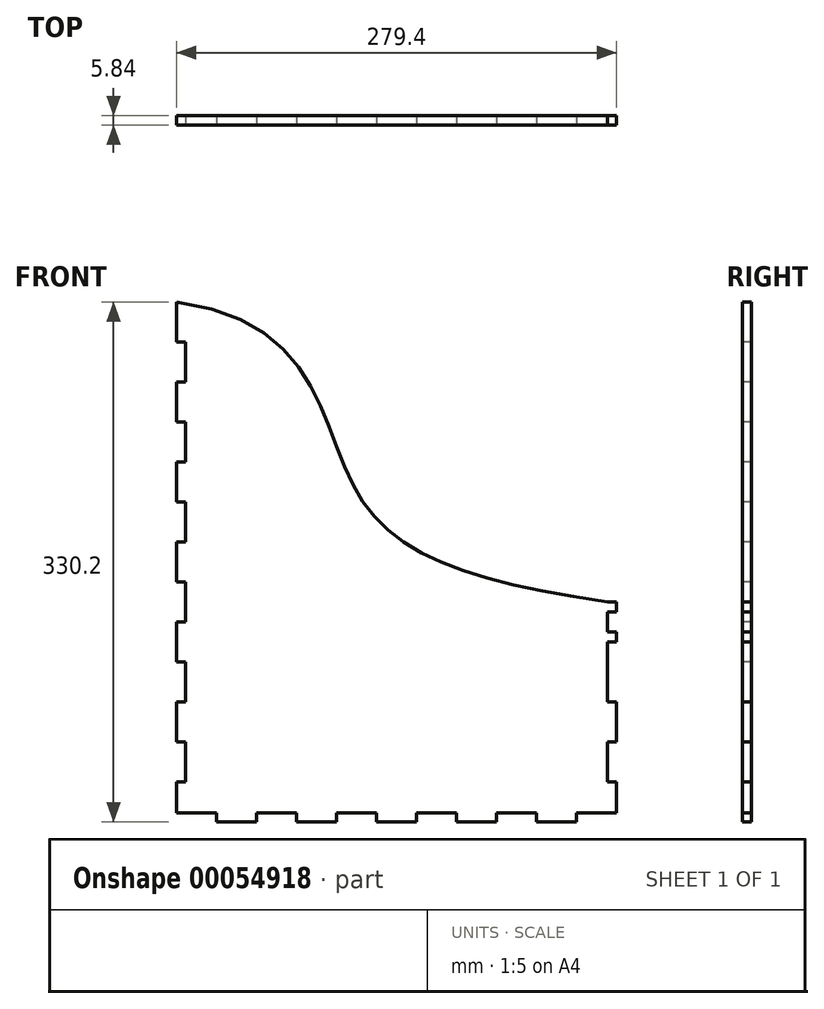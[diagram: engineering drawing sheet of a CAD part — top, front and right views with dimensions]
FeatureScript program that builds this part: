
annotation { "Feature Type Name" : "Feature", "Feature Type Description" : "" }
export const myFeature = defineFeature(function(context is Context, id is Id, definition is map)
    precondition{}
    {
        {
            var Q0;
            Q0=qCreatedBy(makeId("Front.planeOp"),FACE);
            var sketch = newSketch(context, id + "F0", { "sketchPlane" : qUnion([Q0])});
            skLineSegment(sketch, "E0.bottom", {"start": v(-113.95, 205.98) * mm, "end": v(165.45, 205.98) * mm});
            skLineSegment(sketch, "E0.top", {"start": v(-113.95, -124.22) * mm, "end": v(165.45, -124.22) * mm});
            skLineSegment(sketch, "E0.left", {"start": v(-113.95, 205.98) * mm, "end": v(-113.95, -124.22) * mm});
            skLineSegment(sketch, "E0.right", {"start": v(165.45, 205.98) * mm, "end": v(165.45, -124.22) * mm});
            skSolve(sketch);
        }
        {
            var Q0;
            Q0=makeQuery(id+"F0.imprint","IMPRINT",FACE,{"disambiguationData":[TD([[makeQuery(id+"F0.imprint","IMPRINT",EDGE,{"derivedFrom":sQuery(id+"F0.wireOp",EDGE,"E0.bottom")}),-1.0]])]});
            extrude(context, id + "F1", {"entities" : qUnion([Q0]), "depth" : 5.84 * mm});
        }
        {
            var Q0;
            Q0=makeQuery(id+"F1.opExtrude","CAP_FACE",FACE,{"disambiguationData":[OSD([sQuery(id+"F0.wireOp",EDGE,"E0.bottom"),sQuery(id+"F0.wireOp",EDGE,"E0.top"),sQuery(id+"F0.wireOp",EDGE,"E0.left"),sQuery(id+"F0.wireOp",EDGE,"E0.right")])],"isStart":false});
            var sketch = newSketch(context, id + "F2", { "sketchPlane" : qUnion([Q0])});
            skLineSegment(sketch, "E1", {"start": v(165.45, -118.38) * mm, "end": v(140.05, -118.38) * mm});
            skLineSegment(sketch, "E2", {"start": v(140.05, -118.38) * mm, "end": v(140.05, -124.22) * mm});
            skLineSegment(sketch, "E3", {"start": v(140.05, -124.22) * mm, "end": v(114.65, -124.22) * mm});
            skLineSegment(sketch, "E4", {"start": v(114.65, -124.22) * mm, "end": v(114.65, -118.38) * mm});
            skLineSegment(sketch, "E5", {"start": v(114.65, -118.38) * mm, "end": v(89.25, -118.38) * mm});
            skLineSegment(sketch, "E6", {"start": v(89.25, -118.38) * mm, "end": v(89.25, -124.22) * mm});
            skLineSegment(sketch, "E7", {"start": v(89.25, -124.22) * mm, "end": v(63.85, -124.22) * mm});
            skLineSegment(sketch, "E8", {"start": v(63.85, -124.22) * mm, "end": v(63.85, -118.38) * mm});
            skLineSegment(sketch, "E9", {"start": v(63.85, -118.38) * mm, "end": v(38.45, -118.38) * mm});
            skLineSegment(sketch, "E10", {"start": v(38.45, -118.38) * mm, "end": v(38.45, -124.22) * mm});
            skLineSegment(sketch, "E11", {"start": v(38.45, -124.22) * mm, "end": v(13.05, -124.22) * mm});
            skLineSegment(sketch, "E12", {"start": v(13.05, -124.22) * mm, "end": v(13.05, -118.38) * mm});
            skLineSegment(sketch, "E13", {"start": v(13.05, -118.38) * mm, "end": v(-12.35, -118.38) * mm});
            skLineSegment(sketch, "E14", {"start": v(-12.35, -118.38) * mm, "end": v(-12.35, -124.22) * mm});
            skLineSegment(sketch, "E15", {"start": v(-12.35, -124.22) * mm, "end": v(-37.75, -124.22) * mm});
            skLineSegment(sketch, "E16", {"start": v(-37.75, -124.22) * mm, "end": v(-37.75, -118.38) * mm});
            skLineSegment(sketch, "E17", {"start": v(-37.75, -118.38) * mm, "end": v(-113.95, -118.38) * mm});
            skLineSegment(sketch, "E18", {"start": v(-113.95, -118.38) * mm, "end": v(-113.95, -124.22) * mm});
            skLineSegment(sketch, "E19", {"start": v(-113.95, -124.22) * mm, "end": v(-37.75, -124.22) * mm});
            skLineSegment(sketch, "E20.bottom", {"start": v(165.45, -98.82) * mm, "end": v(159.6, -98.82) * mm});
            skLineSegment(sketch, "E20.top", {"start": v(165.45, -73.42) * mm, "end": v(159.6, -73.42) * mm});
            skLineSegment(sketch, "E20.left", {"start": v(165.45, -98.82) * mm, "end": v(165.45, -73.42) * mm});
            skLineSegment(sketch, "E20.right", {"start": v(159.6, -98.82) * mm, "end": v(159.6, -73.42) * mm});
            skLineSegment(sketch, "E21.bottom", {"start": v(165.45, -48.02) * mm, "end": v(159.6, -48.02) * mm});
            skLineSegment(sketch, "E21.top", {"start": v(165.45, -9.92) * mm, "end": v(159.6, -9.92) * mm});
            skLineSegment(sketch, "E21.left", {"start": v(165.45, -48.02) * mm, "end": v(165.45, -9.92) * mm});
            skLineSegment(sketch, "E21.right", {"start": v(159.6, -48.02) * mm, "end": v(159.6, -9.92) * mm});
            skLineSegment(sketch, "E22.bottom", {"start": v(-113.95, -98.82) * mm, "end": v(-108.1, -98.82) * mm});
            skLineSegment(sketch, "E22.top", {"start": v(-113.95, -73.42) * mm, "end": v(-108.1, -73.42) * mm});
            skLineSegment(sketch, "E22.left", {"start": v(-113.95, -98.82) * mm, "end": v(-113.95, -73.42) * mm});
            skLineSegment(sketch, "E22.right", {"start": v(-108.1, -98.82) * mm, "end": v(-108.1, -73.42) * mm});
            skLineSegment(sketch, "E23.bottom", {"start": v(-113.95, -48.02) * mm, "end": v(-108.1, -48.02) * mm});
            skLineSegment(sketch, "E23.top", {"start": v(-113.95, -22.62) * mm, "end": v(-108.1, -22.62) * mm});
            skLineSegment(sketch, "E23.left", {"start": v(-113.95, -48.02) * mm, "end": v(-113.95, -22.62) * mm});
            skLineSegment(sketch, "E23.right", {"start": v(-108.1, -48.02) * mm, "end": v(-108.1, -22.62) * mm});
            skLineSegment(sketch, "E24.bottom", {"start": v(-113.95, 2.78) * mm, "end": v(-108.1, 2.78) * mm});
            skLineSegment(sketch, "E24.top", {"start": v(-113.95, 28.18) * mm, "end": v(-108.1, 28.18) * mm});
            skLineSegment(sketch, "E24.left", {"start": v(-113.95, 2.78) * mm, "end": v(-113.95, 28.18) * mm});
            skLineSegment(sketch, "E24.right", {"start": v(-108.1, 2.78) * mm, "end": v(-108.1, 28.18) * mm});
            skLineSegment(sketch, "E25.bottom", {"start": v(-113.95, 104.38) * mm, "end": v(-108.1, 104.38) * mm});
            skLineSegment(sketch, "E25.top", {"start": v(-113.95, 129.78) * mm, "end": v(-108.1, 129.78) * mm});
            skLineSegment(sketch, "E25.left", {"start": v(-113.95, 104.38) * mm, "end": v(-113.95, 129.78) * mm});
            skLineSegment(sketch, "E25.right", {"start": v(-108.1, 104.38) * mm, "end": v(-108.1, 129.78) * mm});
            skLineSegment(sketch, "E26.bottom", {"start": v(-113.95, 53.58) * mm, "end": v(-108.1, 53.58) * mm});
            skLineSegment(sketch, "E26.top", {"start": v(-113.95, 78.98) * mm, "end": v(-108.1, 78.98) * mm});
            skLineSegment(sketch, "E26.left", {"start": v(-113.95, 53.58) * mm, "end": v(-113.95, 78.98) * mm});
            skLineSegment(sketch, "E26.right", {"start": v(-108.1, 53.58) * mm, "end": v(-108.1, 78.98) * mm});
            skLineSegment(sketch, "E27.bottom", {"start": v(-113.95, 155.18) * mm, "end": v(-108.1, 155.18) * mm});
            skLineSegment(sketch, "E27.top", {"start": v(-113.95, 180.58) * mm, "end": v(-108.1, 180.58) * mm});
            skLineSegment(sketch, "E27.left", {"start": v(-113.95, 155.18) * mm, "end": v(-113.95, 180.58) * mm});
            skLineSegment(sketch, "E27.right", {"start": v(-108.1, 155.18) * mm, "end": v(-108.1, 180.58) * mm});
            skLineSegment(sketch, "E28.bottom", {"start": v(-63.15, -118.38) * mm, "end": v(-88.55, -118.38) * mm});
            skLineSegment(sketch, "E28.top", {"start": v(-63.15, -124.22) * mm, "end": v(-88.55, -124.22) * mm});
            skLineSegment(sketch, "E28.left", {"start": v(-63.15, -118.38) * mm, "end": v(-63.15, -124.22) * mm});
            skLineSegment(sketch, "E28.right", {"start": v(-88.55, -118.38) * mm, "end": v(-88.55, -124.22) * mm});
            skSolve(sketch);
        }
        {
            var Q0;
            {var subQ0=sQuery(id+"F2.wireOp",EDGE,"E1");Q0=makeQuery(id+"F2.imprint","IMPRINT",FACE,{"disambiguationData":[TD([[makeQuery(id+"F2.imprint","IMPRINT",EDGE,{"derivedFrom":subQ0}),1.0]])]});}
            var Q1;
            {var subQ0=sQuery(id+"F2.wireOp",EDGE,"E4");Q1=makeQuery(id+"F2.imprint","IMPRINT",FACE,{"disambiguationData":[TD([[makeQuery(id+"F2.imprint","IMPRINT",EDGE,{"derivedFrom":subQ0}),1.0]])]});}
            var Q2;
            {var subQ0=sQuery(id+"F2.wireOp",EDGE,"E8");Q2=makeQuery(id+"F2.imprint","IMPRINT",FACE,{"disambiguationData":[TD([[makeQuery(id+"F2.imprint","IMPRINT",EDGE,{"derivedFrom":subQ0}),1.0]])]});}
            var Q3;
            {var subQ0=sQuery(id+"F2.wireOp",EDGE,"E12");Q3=makeQuery(id+"F2.imprint","IMPRINT",FACE,{"disambiguationData":[TD([[makeQuery(id+"F2.imprint","IMPRINT",EDGE,{"derivedFrom":subQ0}),1.0]])]});}
            var Q4;
            Q4=makeQuery(id+"F2.imprint","IMPRINT",FACE,{"disambiguationData":[TD([[makeQuery(id+"F2.imprint","IMPRINT",EDGE,{"derivedFrom":sQuery(id+"F2.wireOp",EDGE,"E16")}),1.0]])]});
            var Q5;
            Q5=makeQuery(id+"F2.imprint","IMPRINT",FACE,{"disambiguationData":[TD([[makeQuery(id+"F2.imprint","IMPRINT",EDGE,{"derivedFrom":sQuery(id+"F2.wireOp",EDGE,"E20.bottom")}),-1.0]])]});
            var Q6;
            Q6=makeQuery(id+"F2.imprint","IMPRINT",FACE,{"disambiguationData":[TD([[makeQuery(id+"F2.imprint","IMPRINT",EDGE,{"derivedFrom":sQuery(id+"F2.wireOp",EDGE,"E21.bottom")}),-1.0]])]});
            var Q7;
            Q7=makeQuery(id+"F2.imprint","IMPRINT",FACE,{"disambiguationData":[TD([[makeQuery(id+"F2.imprint","IMPRINT",EDGE,{"derivedFrom":sQuery(id+"F2.wireOp",EDGE,"E22.bottom")}),1.0]])]});
            var Q8;
            Q8=makeQuery(id+"F2.imprint","IMPRINT",FACE,{"disambiguationData":[TD([[makeQuery(id+"F2.imprint","IMPRINT",EDGE,{"derivedFrom":sQuery(id+"F2.wireOp",EDGE,"E23.bottom")}),1.0]])]});
            var Q9;
            Q9=makeQuery(id+"F2.imprint","IMPRINT",FACE,{"disambiguationData":[TD([[makeQuery(id+"F2.imprint","IMPRINT",EDGE,{"derivedFrom":sQuery(id+"F2.wireOp",EDGE,"E24.bottom")}),1.0]])]});
            var Q10;
            Q10=makeQuery(id+"F2.imprint","IMPRINT",FACE,{"disambiguationData":[TD([[makeQuery(id+"F2.imprint","IMPRINT",EDGE,{"derivedFrom":sQuery(id+"F2.wireOp",EDGE,"E26.bottom")}),1.0]])]});
            var Q11;
            Q11=makeQuery(id+"F2.imprint","IMPRINT",FACE,{"disambiguationData":[TD([[makeQuery(id+"F2.imprint","IMPRINT",EDGE,{"derivedFrom":sQuery(id+"F2.wireOp",EDGE,"E27.bottom")}),1.0]])]});
            var Q12;
            Q12=makeQuery(id+"F2.imprint","IMPRINT",FACE,{"disambiguationData":[TD([[makeQuery(id+"F2.imprint","IMPRINT",EDGE,{"derivedFrom":sQuery(id+"F2.wireOp",EDGE,"E25.bottom")}),1.0]])]});
            var Q13;
            {var subQ0=sQuery(id+"F2.wireOp",EDGE,"E18");Q13=makeQuery(id+"F2.imprint","IMPRINT",FACE,{"disambiguationData":[TD([[makeQuery(id+"F2.imprint","IMPRINT",EDGE,{"derivedFrom":subQ0}),1.0]])]});}
            var Q14;
            Q14=makeQuery(id+"F1.opExtrude","CAP_FACE",FACE,{"disambiguationData":[OSD([sQuery(id+"F0.wireOp",EDGE,"E0.bottom"),sQuery(id+"F0.wireOp",EDGE,"E0.top"),sQuery(id+"F0.wireOp",EDGE,"E0.left"),sQuery(id+"F0.wireOp",EDGE,"E0.right")])],"isStart":true});
            extrude(context, id + "F3", {"entities" : qUnion([Q0, Q1, Q2, Q3, Q4, Q5, Q6, Q7, Q8, Q9, Q10, Q11, Q12, Q13]), "operationType" : NewBodyOperationType.REMOVE, "endBound" : BoundingType.UP_TO_SURFACE, "oppositeDirection" : true, "endBoundEntityFace" : qUnion([Q14]), "depth" : 25.4 * mm});
        }
        {
            var Q0;
            Q0=makeQuery(id+"F1.opExtrude","CAP_FACE",FACE,{"disambiguationData":[OSD([sQuery(id+"F0.wireOp",EDGE,"E0.bottom"),sQuery(id+"F0.wireOp",EDGE,"E0.top"),sQuery(id+"F0.wireOp",EDGE,"E0.left"),sQuery(id+"F0.wireOp",EDGE,"E0.right")])],"isStart":false});
            var sketch = newSketch(context, id + "F4", { "sketchPlane" : qUnion([Q0])});
            skPoint(sketch, "E29", {"position": v(-56.8, 205.98) * mm});
            skPoint(sketch, "E30", {"position": v(0.35, 205.98) * mm});
            skPoint(sketch, "E31", {"position": v(57.5, 205.98) * mm});
            skPoint(sketch, "E32", {"position": v(159.6, 15.48) * mm});
            skFitSpline(sketch, "E33", {"points": [v(159.6, 15.48) * mm, v(0, 86.1) * mm, v(-113.95, 205.98) * mm], "startDerivative": vector(-510.53, 75.19) * mm, "endDerivative": vector(-559.98, 77.24) * mm});
            skLineSegment(sketch, "E34", {"start": v(159.6, 15.48) * mm, "end": v(165.45, 15.48) * mm});
            skSolve(sketch);
        }
        {
            var Q0;
            Q0 = qSketchRegion(id + "F4", true);
            var Q1;
            {var subQ0=sQuery(id+"F4.wireOp",EDGE,"E33");Q1=makeQuery(id+"F4.imprint","IMPRINT",FACE,{"disambiguationData":[TD([[makeQuery(id+"F4.imprint","IMPRINT",EDGE,{"derivedFrom":subQ0}),-1.0]])]});}
            var Q2;
            Q2=makeQuery(id+"F1.opExtrude","CAP_FACE",FACE,{"disambiguationData":[OSD([sQuery(id+"F0.wireOp",EDGE,"E0.bottom"),sQuery(id+"F0.wireOp",EDGE,"E0.top"),sQuery(id+"F0.wireOp",EDGE,"E0.left"),sQuery(id+"F0.wireOp",EDGE,"E0.right")])],"isStart":true});
            extrude(context, id + "F5", {"entities" : qUnion([Q0, Q1]), "operationType" : NewBodyOperationType.REMOVE, "endBound" : BoundingType.UP_TO_SURFACE, "oppositeDirection" : true, "endBoundEntityFace" : qUnion([Q2]), "depth" : 25.4 * mm});
        }
        {
            var Q0;
            Q0=makeQuery(id+"F1.opExtrude","CAP_FACE",FACE,{"disambiguationData":[OSD([sQuery(id+"F0.wireOp",EDGE,"E0.bottom"),sQuery(id+"F0.wireOp",EDGE,"E0.top"),sQuery(id+"F0.wireOp",EDGE,"E0.left"),sQuery(id+"F0.wireOp",EDGE,"E0.right")])],"isStart":false});
            var sketch = newSketch(context, id + "F6", { "sketchPlane" : qUnion([Q0])});
            skLineSegment(sketch, "E35.bottom", {"start": v(165.45, -3.57) * mm, "end": v(159.6, -3.57) * mm});
            skLineSegment(sketch, "E35.top", {"start": v(165.45, 9.13) * mm, "end": v(159.6, 9.13) * mm});
            skLineSegment(sketch, "E35.left", {"start": v(165.45, -3.57) * mm, "end": v(165.45, 9.13) * mm});
            skLineSegment(sketch, "E35.right", {"start": v(159.6, -3.57) * mm, "end": v(159.6, 9.13) * mm});
            skSolve(sketch);
        }
        {
            var Q0;
            Q0=makeQuery(id+"F6.imprint","IMPRINT",FACE,{"disambiguationData":[TD([[makeQuery(id+"F6.imprint","IMPRINT",EDGE,{"derivedFrom":sQuery(id+"F6.wireOp",EDGE,"E35.bottom")}),-1.0]])]});
            var Q1;
            Q1=makeQuery(id+"F1.opExtrude","CAP_FACE",FACE,{"disambiguationData":[OSD([sQuery(id+"F0.wireOp",EDGE,"E0.bottom"),sQuery(id+"F0.wireOp",EDGE,"E0.top"),sQuery(id+"F0.wireOp",EDGE,"E0.left"),sQuery(id+"F0.wireOp",EDGE,"E0.right")])],"isStart":true});
            extrude(context, id + "F7", {"entities" : qUnion([Q0]), "operationType" : NewBodyOperationType.REMOVE, "endBound" : BoundingType.UP_TO_SURFACE, "oppositeDirection" : true, "endBoundEntityFace" : qUnion([Q1]), "depth" : 25.4 * mm});
        }
        {
            var Q0;
            Q0=makeQuery(id+"F1.opExtrude","CAP_FACE",FACE,{"disambiguationData":[OSD([sQuery(id+"F0.wireOp",EDGE,"E0.bottom"),sQuery(id+"F0.wireOp",EDGE,"E0.top"),sQuery(id+"F0.wireOp",EDGE,"E0.left"),sQuery(id+"F0.wireOp",EDGE,"E0.right")])],"isStart":false});
            var sketch = newSketch(context, id + "F8", { "sketchPlane" : qUnion([Q0])});
            skCircle(sketch, "E36", {"center": v(-37.75, 190.16) * mm, "radius": 3.18 * mm});
            skSolve(sketch);
        }
        {
            var Q0;
            Q0=makeQuery(id+"F8.imprint","IMPRINT",FACE,{"disambiguationData":[TD([[makeQuery(id+"F8.imprint","IMPRINT",EDGE,{"derivedFrom":sQuery(id+"F8.wireOp",EDGE,"E36")}),1.0]])]});
            var Q1;
            Q1=makeQuery(id+"F1.opExtrude","CAP_FACE",FACE,{"disambiguationData":[OSD([sQuery(id+"F0.wireOp",EDGE,"E0.bottom"),sQuery(id+"F0.wireOp",EDGE,"E0.top"),sQuery(id+"F0.wireOp",EDGE,"E0.left"),sQuery(id+"F0.wireOp",EDGE,"E0.right")])],"isStart":true});
            extrude(context, id + "F9", {"entities" : qUnion([Q0]), "operationType" : NewBodyOperationType.REMOVE, "endBound" : BoundingType.UP_TO_SURFACE, "oppositeDirection" : true, "endBoundEntityFace" : qUnion([Q1]), "depth" : 25.4 * mm});
        }
    });
